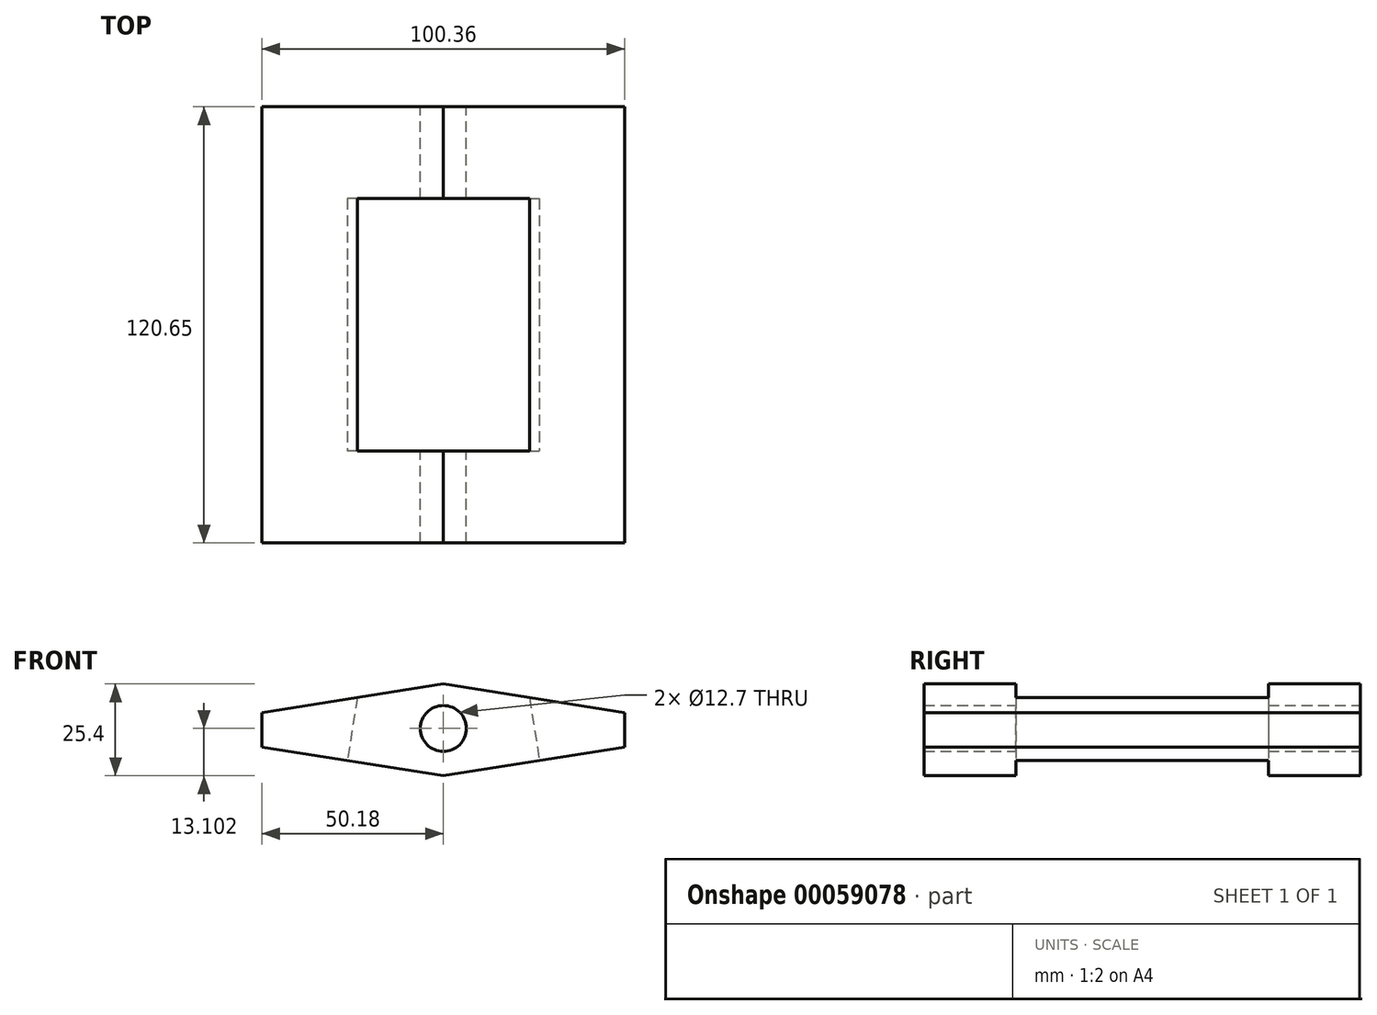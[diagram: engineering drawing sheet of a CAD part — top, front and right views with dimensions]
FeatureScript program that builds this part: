
annotation { "Feature Type Name" : "Feature", "Feature Type Description" : "" }
export const myFeature = defineFeature(function(context is Context, id is Id, definition is map)
    precondition{}
    {
        {
            var Q0;
            Q0=qCreatedBy(makeId("Front.planeOp"),FACE);
            var sketch = newSketch(context, id + "F0", { "sketchPlane" : qUnion([Q0])});
            skLineSegment(sketch, "E0", {"start": v(-50.18, -8.84) * mm, "end": v(-50.18, 0.69) * mm});
            skLineSegment(sketch, "E1", {"start": v(-50.18, 0.69) * mm, "end": v(0, 8.62) * mm});
            skLineSegment(sketch, "E2", {"start": v(0, 8.62) * mm, "end": v(0, -16.78) * mm});
            skLineSegment(sketch, "E3", {"start": v(0, -16.78) * mm, "end": v(-50.18, -8.84) * mm});
            skLineSegment(sketch, "E4", {"start": v(0, 8.62) * mm, "end": v(50.18, 0.69) * mm});
            skLineSegment(sketch, "E5", {"start": v(50.18, 0.69) * mm, "end": v(50.18, -8.84) * mm});
            skLineSegment(sketch, "E6", {"start": v(0, -16.78) * mm, "end": v(50.18, -8.84) * mm});
            skSolve(sketch);
        }
        {
            var Q0;
            Q0=makeQuery(id+"F0.imprint","IMPRINT",FACE,{"disambiguationData":[TD([[makeQuery(id+"F0.imprint","IMPRINT",EDGE,{"derivedFrom":sQuery(id+"F0.wireOp",EDGE,"E0")}),-1.0]])]});
            extrude(context, id + "F1", {"entities" : qUnion([Q0]), "depth" : 120.65 * mm});
        }
        {
            var Q0;
            Q0=makeQuery(id+"F0.imprint","IMPRINT",FACE,{"disambiguationData":[TD([[makeQuery(id+"F0.imprint","IMPRINT",EDGE,{"derivedFrom":sQuery(id+"F0.wireOp",EDGE,"E2")}),1.0]])]});
            extrude(context, id + "F2", {"entities" : qUnion([Q0]), "operationType" : NewBodyOperationType.ADD, "depth" : 120.65 * mm});
        }
        {
            var Q0;
            Q0=qCreatedBy(makeId("Front.planeOp"),FACE);
            var sketch = newSketch(context, id + "F3", { "sketchPlane" : qUnion([Q0])});
            skCircle(sketch, "E7", {"center": v(0, -3.68) * mm, "radius": 6.35 * mm});
            skSolve(sketch);
        }
        {
            var Q0;
            Q0=sQuery(id+"F3.wireOp",VERTEX,"E7.center");
            var Q1;
            Q1=makeQuery(id+"F1.opExtrude","SWEPT_BODY",BODY,{"disambiguationData":[OSD([sQuery(id+"F0.wireOp",EDGE,"E0"),sQuery(id+"F0.wireOp",EDGE,"E1"),sQuery(id+"F0.wireOp",EDGE,"E2"),sQuery(id+"F0.wireOp",EDGE,"E3")])]});
            hole(context, id + "F4", {"style" : HoleStyle.SIMPLE, "holeDiameter" : 12.7 * mm, "endStyle" : HoleEndStyle.THROUGH, "oppositeDirection" : true, "locations" : qUnion([Q0]), "scope" : qUnion([Q1])});
        }
        {
            var Q0;
            Q0=makeQuery(id+"F2.opExtrude","SWEPT_FACE",FACE,{"disambiguationData":[OSD([sQuery(id+"F0.wireOp",EDGE,"E6")])]});
            var sketch = newSketch(context, id + "F5", { "sketchPlane" : qUnion([Q0])});
            skLineSegment(sketch, "E8.left", {"start": v(-2.62, 25.4) * mm, "end": v(-2.62, 101.6) * mm});
            skLineSegment(sketch, "E9.bottom", {"start": v(-2.62, 25.4) * mm, "end": v(24.27, 25.4) * mm});
            skLineSegment(sketch, "E9.top", {"start": v(-2.62, 95.25) * mm, "end": v(24.27, 95.25) * mm});
            skLineSegment(sketch, "E9.left", {"start": v(-2.62, 25.4) * mm, "end": v(-2.62, 95.25) * mm});
            skLineSegment(sketch, "E9.right", {"start": v(24.27, 25.4) * mm, "end": v(24.27, 95.25) * mm});
            skSolve(sketch);
        }
        {
            var Q0;
            Q0=makeQuery(id+"F1.opExtrude","SWEPT_FACE",FACE,{"disambiguationData":[OSD([sQuery(id+"F0.wireOp",EDGE,"E3")])]});
            var sketch = newSketch(context, id + "F6", { "sketchPlane" : qUnion([Q0])});
            skLineSegment(sketch, "E10.left", {"start": v(2.62, 25.4) * mm, "end": v(2.62, 95.25) * mm});
            skLineSegment(sketch, "E11.bottom", {"start": v(2.62, 25.4) * mm, "end": v(-24.27, 25.4) * mm});
            skLineSegment(sketch, "E11.top", {"start": v(2.62, 95.25) * mm, "end": v(-24.27, 95.25) * mm});
            skLineSegment(sketch, "E11.right", {"start": v(-24.27, 25.4) * mm, "end": v(-24.27, 95.25) * mm});
            skSolve(sketch);
        }
        {
            var Q0;
            Q0=makeQuery(id+"F6.imprint","IMPRINT",FACE,{"disambiguationData":[TD([[makeQuery(id+"F6.imprint","IMPRINT",EDGE,{"derivedFrom":sQuery(id+"F6.wireOp",EDGE,"E11.bottom")}),-1.0]])]});
            extrude(context, id + "F7", {"entities" : qUnion([Q0]), "operationType" : NewBodyOperationType.REMOVE, "endBound" : BoundingType.THROUGH_ALL, "oppositeDirection" : true, "depth" : 25.4 * mm});
        }
        {
            var Q0;
            Q0=makeQuery(id+"F5.imprint","IMPRINT",FACE,{"disambiguationData":[TD([[makeQuery(id+"F5.imprint","IMPRINT",EDGE,{"derivedFrom":sQuery(id+"F5.wireOp",EDGE,"E9.bottom")}),1.0]])]});
            extrude(context, id + "F8", {"entities" : qUnion([Q0]), "operationType" : NewBodyOperationType.REMOVE, "endBound" : BoundingType.THROUGH_ALL, "oppositeDirection" : true, "depth" : 25.4 * mm});
        }
    });
